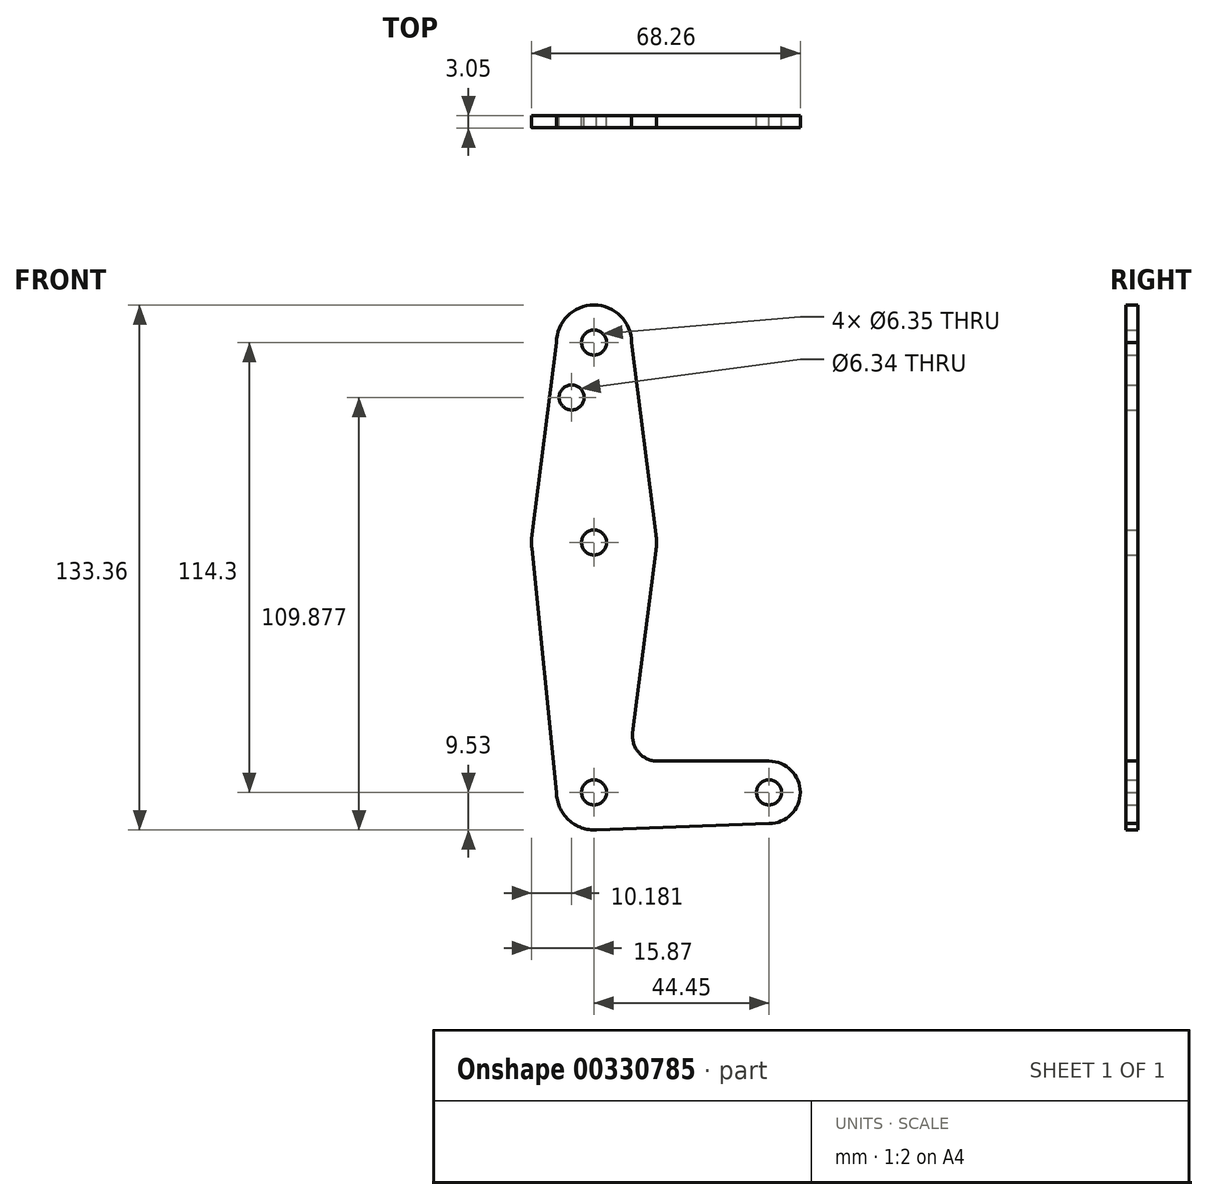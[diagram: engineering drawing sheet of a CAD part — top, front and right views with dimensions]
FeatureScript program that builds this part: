
annotation { "Feature Type Name" : "Feature", "Feature Type Description" : "" }
export const myFeature = defineFeature(function(context is Context, id is Id, definition is map)
    precondition{}
    {
        {
            var Q0;
            Q0=qCreatedBy(makeId("Front.planeOp"),FACE);
            var sketch = newSketch(context, id + "F0", { "sketchPlane" : qUnion([Q0])});
            skCircle(sketch, "E0", {"center": v(0, 114.3) * mm, "radius": 9.53 * mm});
            skCircle(sketch, "E1", {"center": v(0, 63.5) * mm, "radius": 15.88 * mm});
            skCircle(sketch, "E2", {"center": v(0, 0) * mm, "radius": 9.53 * mm});
            skLineSegment(sketch, "E3", {"start": v(0, 0) * mm, "end": v(44.45, 0) * mm, "construction": true});
            skCircle(sketch, "E4", {"center": v(44.45, 0) * mm, "radius": 7.94 * mm});
            skCircle(sketch, "E5", {"center": v(0, 114.3) * mm, "radius": 3.18 * mm});
            skCircle(sketch, "E6", {"center": v(0, 63.5) * mm, "radius": 3.18 * mm});
            skCircle(sketch, "E7", {"center": v(0, 0) * mm, "radius": 3.18 * mm});
            skCircle(sketch, "E8", {"center": v(44.45, 0) * mm, "radius": 3.18 * mm});
            skLineSegment(sketch, "E9", {"start": v(0, 114.3) * mm, "end": v(0, 0) * mm, "construction": true});
            skLineSegment(sketch, "E10", {"start": v(-9.53, 114.3) * mm, "end": v(-15.75, 65.5) * mm});
            skLineSegment(sketch, "E11", {"start": v(9.52, 114.3) * mm, "end": v(15.75, 65.5) * mm});
            skLineSegment(sketch, "E12", {"start": v(0, -9.52) * mm, "end": v(44.45, -7.94) * mm});
            skCircle(sketch, "E13", {"center": v(-5.69, 100.35) * mm, "radius": 3.17 * mm});
            skLineSegment(sketch, "E14", {"start": v(15.75, 61.5) * mm, "end": v(9.83, 15.1) * mm});
            skLineSegment(sketch, "E15", {"start": v(16.13, 7.94) * mm, "end": v(44.45, 7.94) * mm});
            skArc(sketch, "E16.filletArc", {"start": v(9.83, 15.1) * mm, "mid": v(11.36, 10.1) * mm, "end": v(16.13, 7.94) * mm});
            skLineSegment(sketch, "E17", {"start": v(-9.53, 0) * mm, "end": v(-15.96, 63.5) * mm});
            skSolve(sketch);
        }
        {
            var Q0;
            Q0 = qSketchRegion(id + "F0", true);
            extrude(context, id + "F1", {"entities" : qUnion([Q0]), "depth" : 3.05 * mm});
        }
    });
